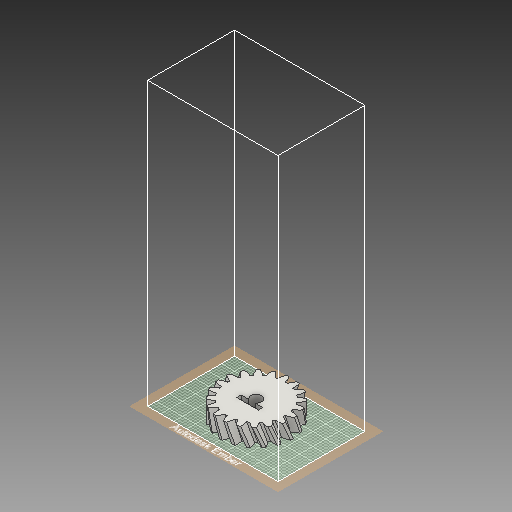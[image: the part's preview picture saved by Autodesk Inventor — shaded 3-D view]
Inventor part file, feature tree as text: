
AUTODESK INVENTOR PART (.ipt)
format: ipt  version: 2017 SP1 (Build 210196100, 196)  size: 846,848 bytes
history: native  units: mm (DEFAULTED — no unit token found)
features: plane x3, other x3, sketch x3, extrude x2
ambient origin geometry x8: Origin, YZ Plane, XZ Plane, XY Plane, X Axis, Y Axis, Z Axis, Center Point
bodies: Solid1 (feature_tree)
feature tree (11):
  extrude  "Extrusion1"  Depth=7.0mm TaperAngle=0.0deg
  plane  "Work Plane2"
  plane  "Work Plane8"
  plane  "Work Plane9"
  other  "Engrenage cylindrique"
  extrude  "Extrusion2"  Depth=10.0mm TaperAngle=0.0deg
  sketch  "Sketch1"  dims[d0=32.749068mm d1=7.0mm d2=0.0mm]
  sketch  "Sketch2"  dims[d3=30.066593mm d4=10.0mm d5=0.0mm d16=30.066593mm d17=0.0mm d34=1.570796mm d39=0.0mm d41=0.0mm d43=30.066593mm d46=30.066593mm d47=0.0mm d48=0.0mm d49=5.0mm d50=10.0mm d51=5.0mm d52=2.0mm d53=2.0mm d54=8.0mm d55=0.0mm]
  other  "Srf1"
  sketch  "Esquisse3"
  other  "Diamètre primitif"
